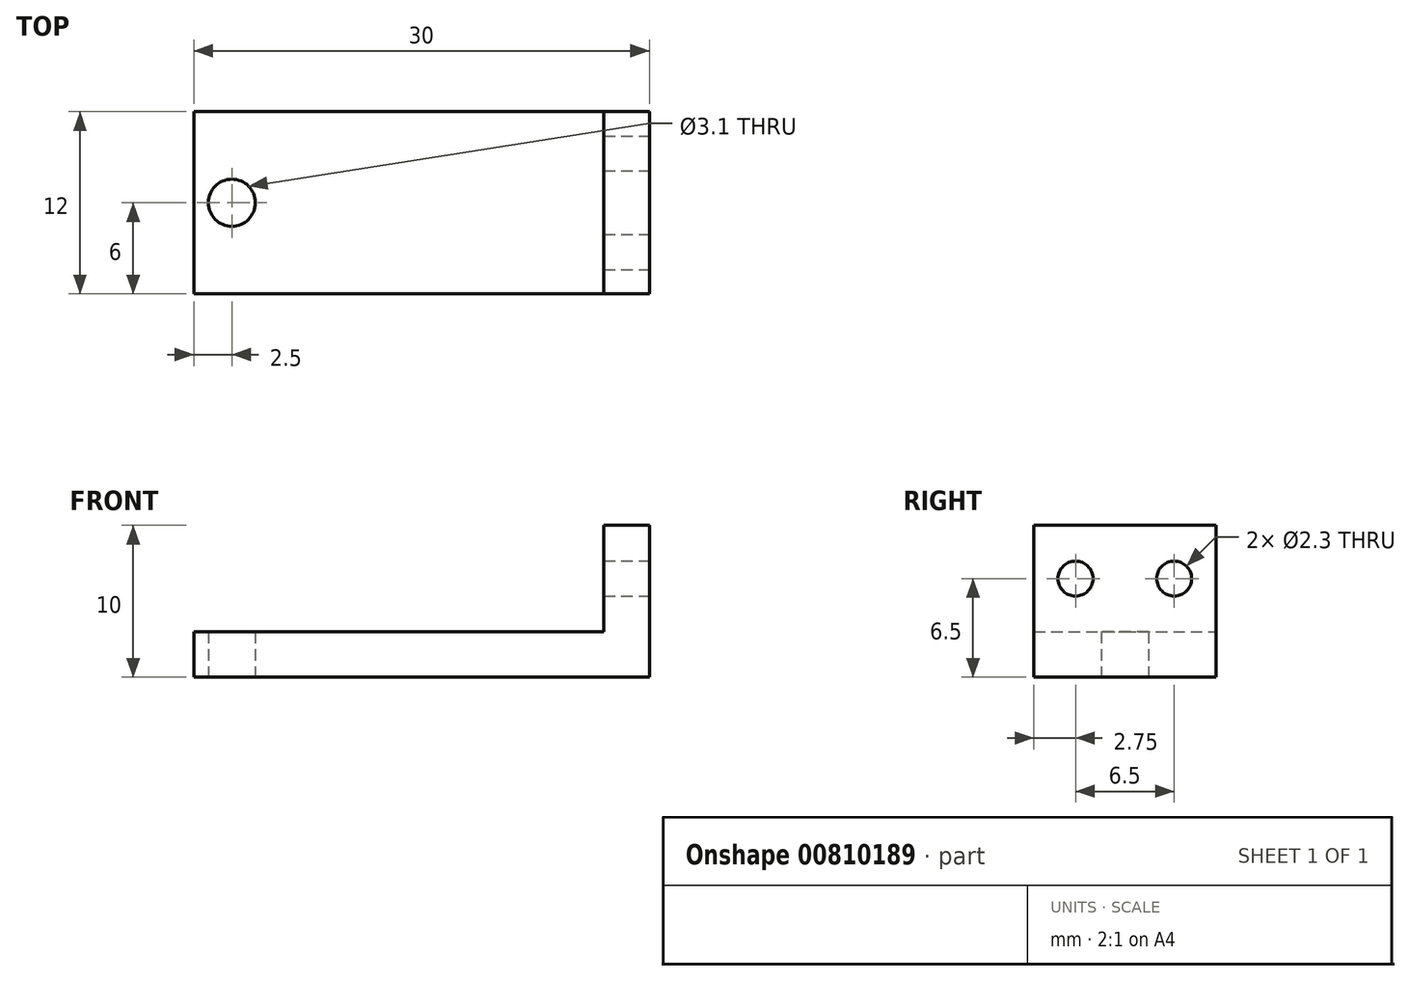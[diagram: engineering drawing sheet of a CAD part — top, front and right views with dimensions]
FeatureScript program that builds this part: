
annotation { "Feature Type Name" : "Feature", "Feature Type Description" : "" }
export const myFeature = defineFeature(function(context is Context, id is Id, definition is map)
    precondition{}
    {
        {
            var Q0;
            Q0=qCreatedBy(makeId("Top.planeOp"),FACE);
            var sketch = newSketch(context, id + "F0", { "sketchPlane" : qUnion([Q0])});
            skLineSegment(sketch, "E0.bottom", {"start": v(15, 6) * mm, "end": v(-15, 6) * mm});
            skLineSegment(sketch, "E0.top", {"start": v(15, -6) * mm, "end": v(-15, -6) * mm});
            skLineSegment(sketch, "E0.left", {"start": v(15, 6) * mm, "end": v(15, -6) * mm});
            skLineSegment(sketch, "E0.right", {"start": v(-15, 6) * mm, "end": v(-15, -6) * mm});
            skPoint(sketch, "E0.middle", {"position": v(0, 0) * mm});
            skCircle(sketch, "E1", {"center": v(-12.5, 0) * mm, "radius": 1.55 * mm});
            skSolve(sketch);
        }
        {
            var Q0;
            Q0 = qSketchRegion(id + "F0", true);
            extrude(context, id + "F1", {"entities" : qUnion([Q0]), "depth" : 3 * mm, "offsetDistance" : 25 * mm});
        }
        {
            var Q0;
            Q0=makeQuery(id+"F1.opExtrude","SWEPT_FACE",FACE,{"disambiguationData":[OSD([sQuery(id+"F0.wireOp",EDGE,"E0.left")])]});
            var sketch = newSketch(context, id + "F2", { "sketchPlane" : qUnion([Q0])});
            skLineSegment(sketch, "E2.bottom", {"start": v(-6, 0) * mm, "end": v(6, 0) * mm});
            skLineSegment(sketch, "E2.top", {"start": v(-6, 10) * mm, "end": v(6, 10) * mm});
            skLineSegment(sketch, "E2.left", {"start": v(-6, 0) * mm, "end": v(-6, 10) * mm});
            skLineSegment(sketch, "E2.right", {"start": v(6, 0) * mm, "end": v(6, 10) * mm});
            skCircle(sketch, "E3", {"center": v(-3.25, 6.5) * mm, "radius": 1.15 * mm});
            skCircle(sketch, "E4", {"center": v(3.25, 6.5) * mm, "radius": 1.15 * mm});
            skSolve(sketch);
        }
        {
            var Q0;
            Q0 = qSketchRegion(id + "F2", true);
            extrude(context, id + "F3", {"entities" : qUnion([Q0]), "operationType" : NewBodyOperationType.ADD, "oppositeDirection" : true, "depth" : 3 * mm, "offsetDistance" : 25 * mm});
        }
    });
